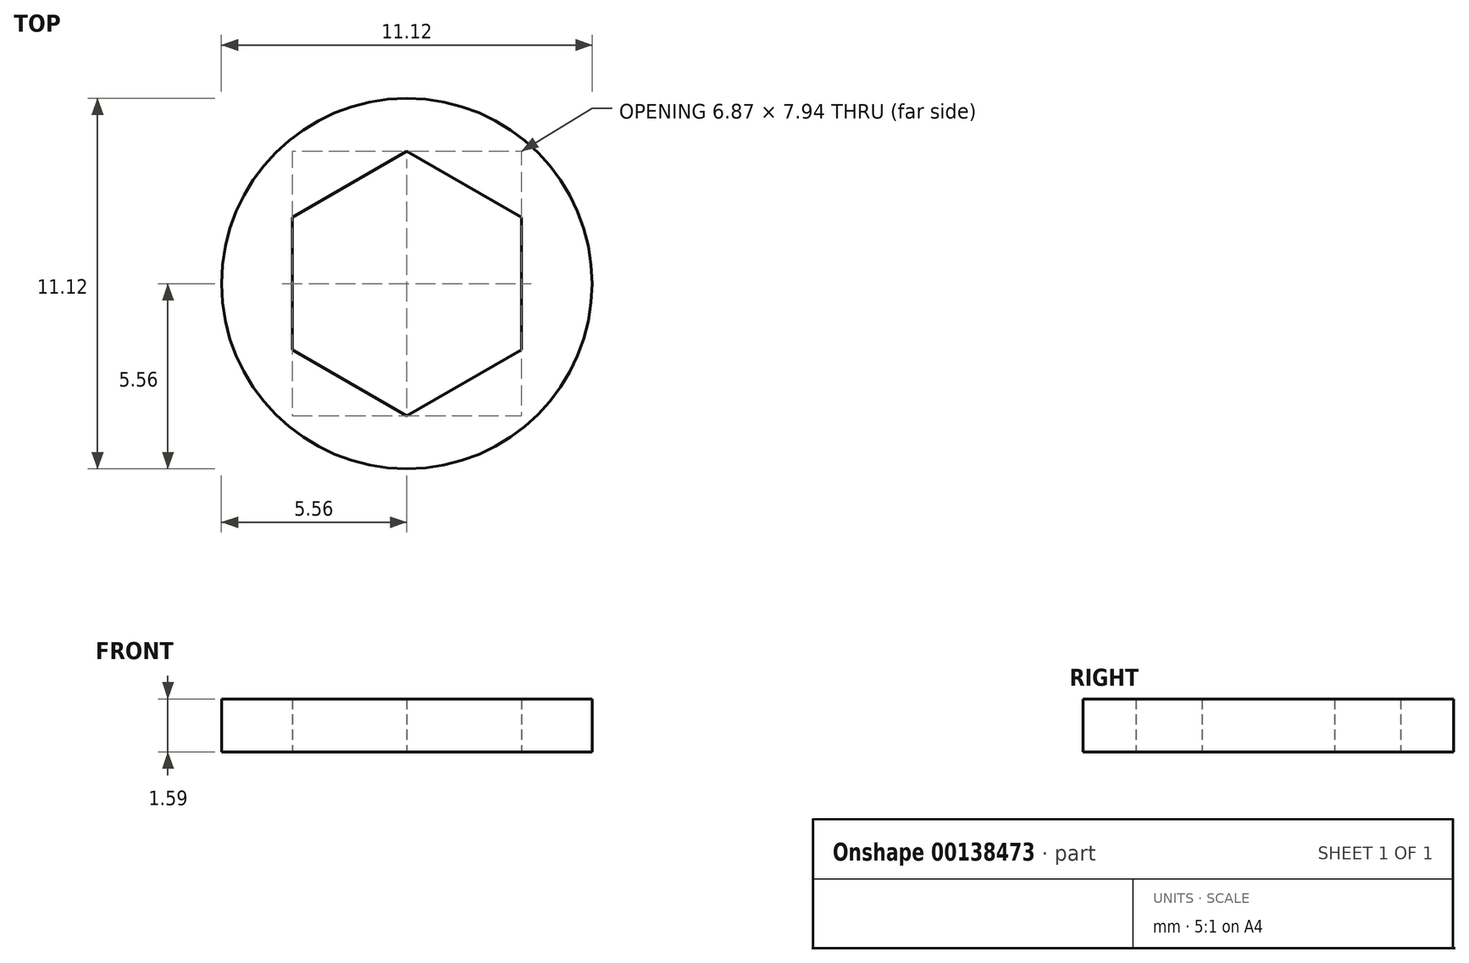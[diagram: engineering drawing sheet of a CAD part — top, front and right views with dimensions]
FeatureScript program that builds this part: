
annotation { "Feature Type Name" : "Feature", "Feature Type Description" : "" }
export const myFeature = defineFeature(function(context is Context, id is Id, definition is map)
    precondition{}
    {
        {
            var Q0;
            Q0=qCreatedBy(makeId("Top.planeOp"),FACE);
            var sketch = newSketch(context, id + "F0", { "sketchPlane" : qUnion([Q0])});
            skCircle(sketch, "E0.cCircle", {"center": v(0, 0) * mm, "radius": 3.97 * mm, "construction": true});
            skLineSegment(sketch, "E0.0", {"start": v(0, -3.97) * mm, "end": v(-3.44, -1.98) * mm});
            skLineSegment(sketch, "E0.1", {"start": v(-3.44, -1.98) * mm, "end": v(-3.44, 1.98) * mm});
            skLineSegment(sketch, "E0.2", {"start": v(-3.44, 1.98) * mm, "end": v(0, 3.97) * mm});
            skLineSegment(sketch, "E0.3", {"start": v(0, 3.97) * mm, "end": v(3.44, 1.98) * mm});
            skLineSegment(sketch, "E0.4", {"start": v(3.44, 1.98) * mm, "end": v(3.44, -1.98) * mm});
            skLineSegment(sketch, "E0.5", {"start": v(3.44, -1.98) * mm, "end": v(0, -3.97) * mm});
            skCircle(sketch, "E1", {"center": v(0, 0) * mm, "radius": 5.56 * mm});
            skSolve(sketch);
        }
        {
            var Q0;
            Q0 = qSketchRegion(id + "F0", true);
            extrude(context, id + "F1", {"entities" : qUnion([Q0]), "depth" : 1.59 * mm});
        }
    });
